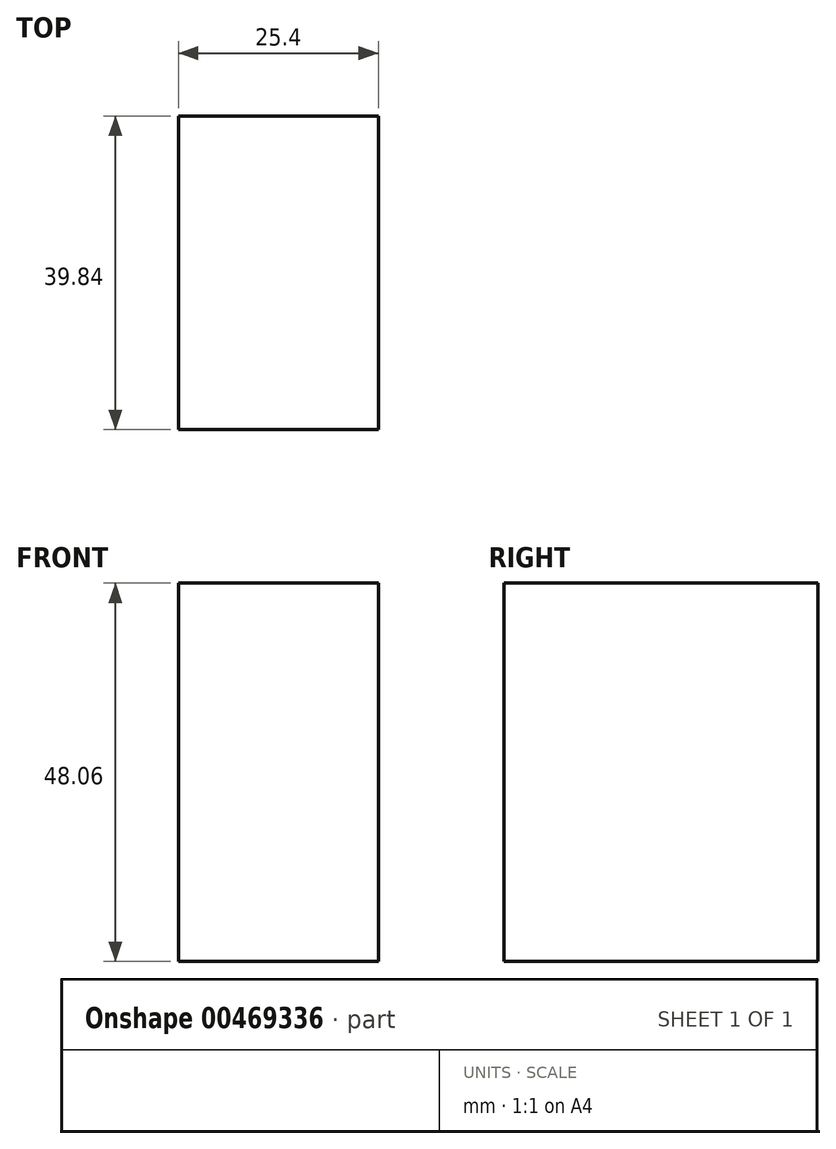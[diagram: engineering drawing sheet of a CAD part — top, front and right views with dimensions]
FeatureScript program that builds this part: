
annotation { "Feature Type Name" : "Feature", "Feature Type Description" : "" }
export const myFeature = defineFeature(function(context is Context, id is Id, definition is map)
    precondition{}
    {
        {
            var Q0;
            Q0=qCreatedBy(makeId("Right.planeOp"),FACE);
            var sketch = newSketch(context, id + "F0", { "sketchPlane" : qUnion([Q0])});
            skLineSegment(sketch, "E0.bottom", {"start": v(-39.92, 0) * mm, "end": v(-41.98, 0) * mm});
            skLineSegment(sketch, "E0.top", {"start": v(-39.92, -23.36) * mm, "end": v(-41.98, -23.36) * mm});
            skLineSegment(sketch, "E0.left", {"start": v(-39.92, 0) * mm, "end": v(-39.92, -23.36) * mm});
            skLineSegment(sketch, "E0.right", {"start": v(-41.98, 0) * mm, "end": v(-41.98, -23.36) * mm});
            skPoint(sketch, "E1.firstSnap0", {"position": v(-39.92, -11.68) * mm});
            skLineSegment(sketch, "E1.bottom", {"start": v(-20.71, -11.68) * mm, "end": v(19.13, -11.68) * mm});
            skLineSegment(sketch, "E1.top", {"start": v(-20.71, -59.74) * mm, "end": v(19.13, -59.74) * mm});
            skLineSegment(sketch, "E1.left", {"start": v(-20.71, -11.68) * mm, "end": v(-20.71, -59.74) * mm});
            skLineSegment(sketch, "E1.right", {"start": v(19.13, -11.68) * mm, "end": v(19.13, -59.74) * mm});
            skSolve(sketch);
        }
        {
            var Q0;
            Q0=makeQuery(id+"F0.imprint","IMPRINT",FACE,{"disambiguationData":[TD([[makeQuery(id+"F0.imprint","IMPRINT",EDGE,{"derivedFrom":sQuery(id+"F0.wireOp",EDGE,"E1.bottom")}),-1.0]])]});
            extrude(context, id + "F1", {"entities" : qUnion([Q0]), "depth" : 25.4 * mm});
        }
    });
